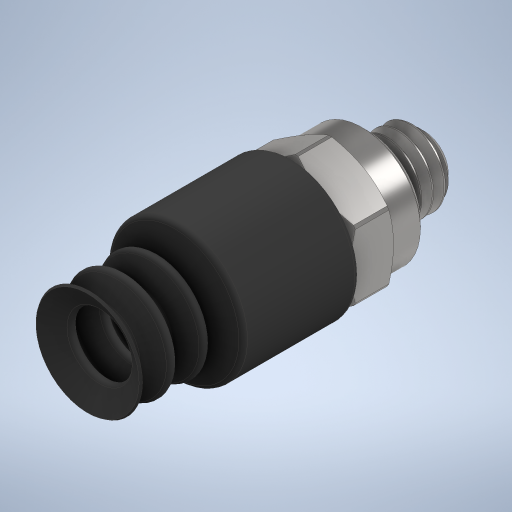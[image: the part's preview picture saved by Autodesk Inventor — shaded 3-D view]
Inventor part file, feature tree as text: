
AUTODESK INVENTOR PART (.ipt)
format: ipt  version: 2023 (Build 270158000, 158)  size: 599,552 bytes
history: native  units: in
note: dims shown in document units (in); Inventor stores cm internally (conversion verified against a paired STEP export)
features: revolve x2, other x1
ambient origin geometry x8: Origin, YZ Plane, XZ Plane, XY Plane, X Axis, Y Axis, Z Axis, Center Point
bodies: Solid1 (feature_tree), Solid2 (feature_tree), Solid3 (feature_tree)
feature tree (3):
  revolve  "Revolve1"  [1 undecoded]
  other  "Boss-Extrude3"
  revolve  "Revolve3"  [1 undecoded]
note: 2 required parameter values undecoded (feature->parameter linkage not recoverable at this tier; creation-order binding heuristic only, values carry confidence <= 0.55)
